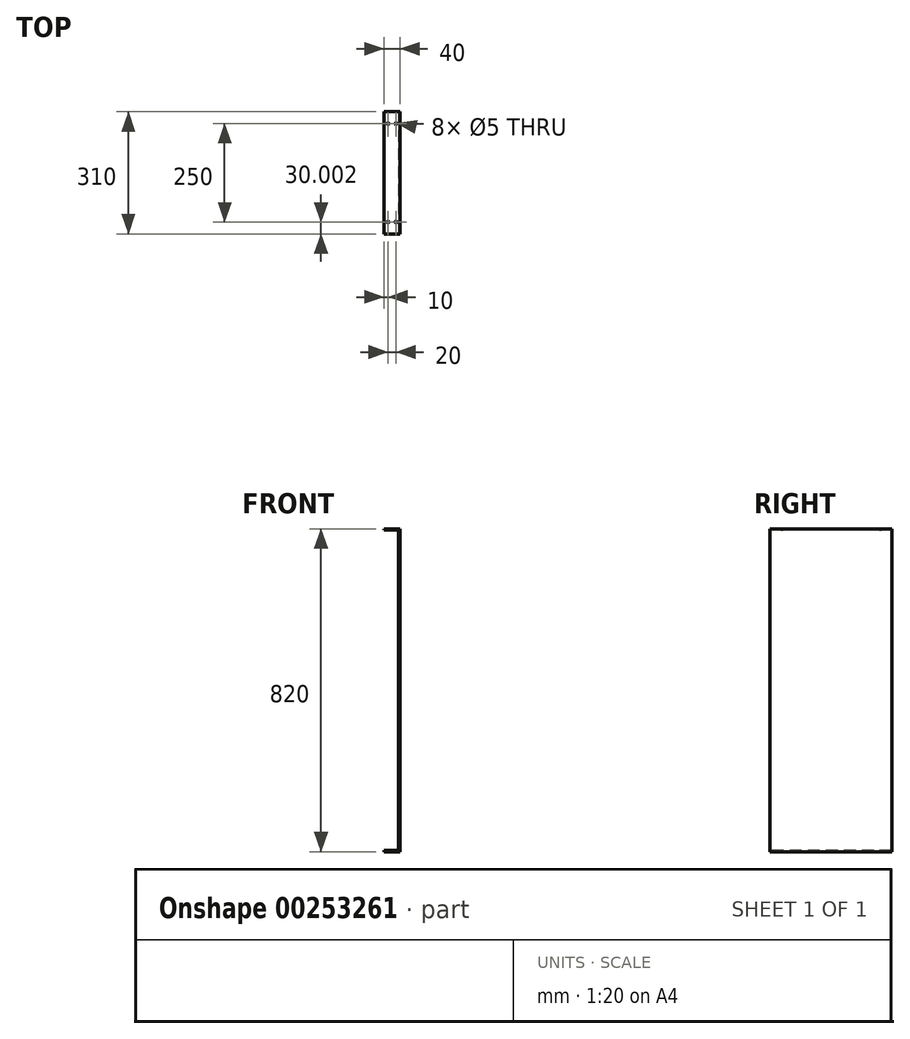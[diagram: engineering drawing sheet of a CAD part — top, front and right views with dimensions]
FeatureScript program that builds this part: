
annotation { "Feature Type Name" : "Feature", "Feature Type Description" : "" }
export const myFeature = defineFeature(function(context is Context, id is Id, definition is map)
    precondition{}
    {
        {
            var Q0;
            Q0=qCreatedBy(makeId("Top.planeOp"),FACE);
            var sketch = newSketch(context, id + "F0", { "sketchPlane" : qUnion([Q0])});
            skLineSegment(sketch, "E0", {"start": v(-40, 214.26) * mm, "end": v(0, 214.26) * mm});
            skLineSegment(sketch, "E1", {"start": v(0, 214.26) * mm, "end": v(0, -95.74) * mm});
            skLineSegment(sketch, "E2", {"start": v(0, -95.74) * mm, "end": v(-40, -95.74) * mm});
            skLineSegment(sketch, "E3", {"start": v(-40, 214.26) * mm, "end": v(-40, -95.74) * mm});
            skSolve(sketch);
        }
        {
            var Q0;
            Q0 = qSketchRegion(id + "F0", true);
            extrude(context, id + "F1", {"entities" : qUnion([Q0]), "depth" : 820 * mm});
        }
        {
            var Q0;
            Q0=makeQuery(id+"F1.opExtrude","SWEPT_FACE",FACE,{"disambiguationData":[OSD([sQuery(id+"F0.wireOp",EDGE,"E0")])]});
            var Q1;
            Q1=makeQuery(id+"F1.opExtrude","SWEPT_FACE",FACE,{"disambiguationData":[OSD([sQuery(id+"F0.wireOp",EDGE,"E2")])]});
            var Q2;
            Q2=makeQuery(id+"F1.opExtrude","SWEPT_FACE",FACE,{"disambiguationData":[OSD([sQuery(id+"F0.wireOp",EDGE,"E3")])]});
            shell(context, id + "F2", {"entities" : qUnion([Q0, Q1, Q2]), "thickness" : 3 * mm});
        }
        {
            var Q0;
            Q0=makeQuery(id+"F1.opExtrude","CAP_FACE",FACE,{"disambiguationData":[OSD([sQuery(id+"F0.wireOp",EDGE,"E0"),sQuery(id+"F0.wireOp",EDGE,"E1"),sQuery(id+"F0.wireOp",EDGE,"E2"),sQuery(id+"F0.wireOp",EDGE,"E3")])],"isStart":false});
            var sketch = newSketch(context, id + "F3", { "sketchPlane" : qUnion([Q0])});
            skCircle(sketch, "E4", {"center": v(-30, 184.26) * mm, "radius": 2.5 * mm});
            skCircle(sketch, "E5", {"center": v(-10, 184.26) * mm, "radius": 2.5 * mm});
            skLineSegment(sketch, "E6", {"start": v(-40, 59.26) * mm, "end": v(29.42, 59.26) * mm, "construction": true});
            skCircle(sketch, "E7.MirrorC", {"center": v(-30, -65.74) * mm, "radius": 2.5 * mm});
            skCircle(sketch, "E8.MirrorC", {"center": v(-10, -65.74) * mm, "radius": 2.5 * mm});
            skSolve(sketch);
        }
        {
            var Q0;
            Q0 = qSketchRegion(id + "F3", true);
            extrude(context, id + "F4", {"entities" : qUnion([Q0]), "operationType" : NewBodyOperationType.REMOVE, "endBound" : BoundingType.THROUGH_ALL, "oppositeDirection" : true, "depth" : 25 * mm});
        }
    });
